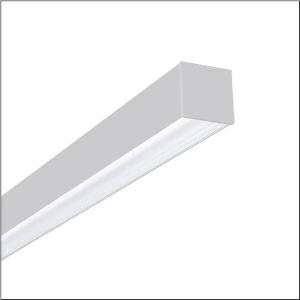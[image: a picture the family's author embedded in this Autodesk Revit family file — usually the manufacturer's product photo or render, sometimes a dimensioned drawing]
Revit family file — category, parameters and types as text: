
# Revit family: silica_r_5mx31bd2w4a_93b3
name_source: partatom
category: Lighting Fixtures
units: mm (PartAtom-declared; Revit-internal decimal feet)

## family parameters
Cut with Voids When Loaded = No
Host = Face
Light Source = No
Part Type = Normal
Room Calculation Point = No
Round Connector Dimension = Use Diameter
Shared = No

## types (1)
- --- (1 x LED, 14160 lm, 92.6 W, 4000K)
    Apparent Load = 93 VA
    CIE Flux Codes = 82 97 100 70 100
    Color Rendering = 80
    Color Temperature = 4000K
    Default Elevation = 1800 mm
    Description = Silica®, office luminaire, of aluminium, light emission: direct/indirect distribution, primary light characteristic: symmetric, installation type: suspended mounting, LED, rated luminous flux: 14.160lm, luminous efficacy: 153lm/W, light colour: 840, colour temperature: 4000K, control gear: ECG DALI, with terminal, 3+2-pole, max. 2.5mm², mains connection: 230V, AC, 50/60Hz, connection cable inclusive, cable length: 1,5m, rated input power: 93W, luminaire housing, of aluminium, traffic white (RAL 9016), length: 2.844mm, width: 65mm, height: 64mm, protection rating (complete): IP20, insulation class (complete): insulation class I (protective earthing), certification: CE, permissible operating ambient temperature: 0..+35°C, standard: EN 50419, packaging unit: 1 piece
    Height = 64 mm
    Lamp = 1 x LED
    Lamp Light Flux = 14160 lm
    Lamp Power = 92.6 W
    Lamp count = 1
    Length = 2845 mm
    Luminous efficacy = 153 lm/W
    Manufacturer = Siteco
    ModVariant = No
    Model = 5MX31BD2W4A
    Mounting Place = Ceiling
    Mounting Type = Pendant
    Number of Poles = 1
    OnlyDefault = Yes
    Power Factor = 1
    Product Name = Silica®
    Product group = office luminaire | ceiling pendant
    ProductGroupID = 902
    Protection Class = Protection class I
    Protection Degree = IP 20
    RLX_Detail_Level = 1
    RLX_Emergency_Light_Flux = 0 lm
    RLX_Emergency_Type = 0
    RLX_Emergency_Type_DB = No
    RlxData = <blob elided: 28865 chars, md5=25a74552>
    Socket = socket
    Standby Power = 0 W
    System Light Flux = 14160 lm
    System Power = 93 W
    Type Comments = factory setting: direct and indirect light
    Type Image = l_1003924.jpg
    URL = http://relux.com
    VarID = @adj_138212
    Voltage = 0 V
    Weight = 0.00 kg
    Width = 66 mm

## geometry (parser evidence)
native form markers: Blend x4, Sweep x13
no freeform markers — native parametric forms only
